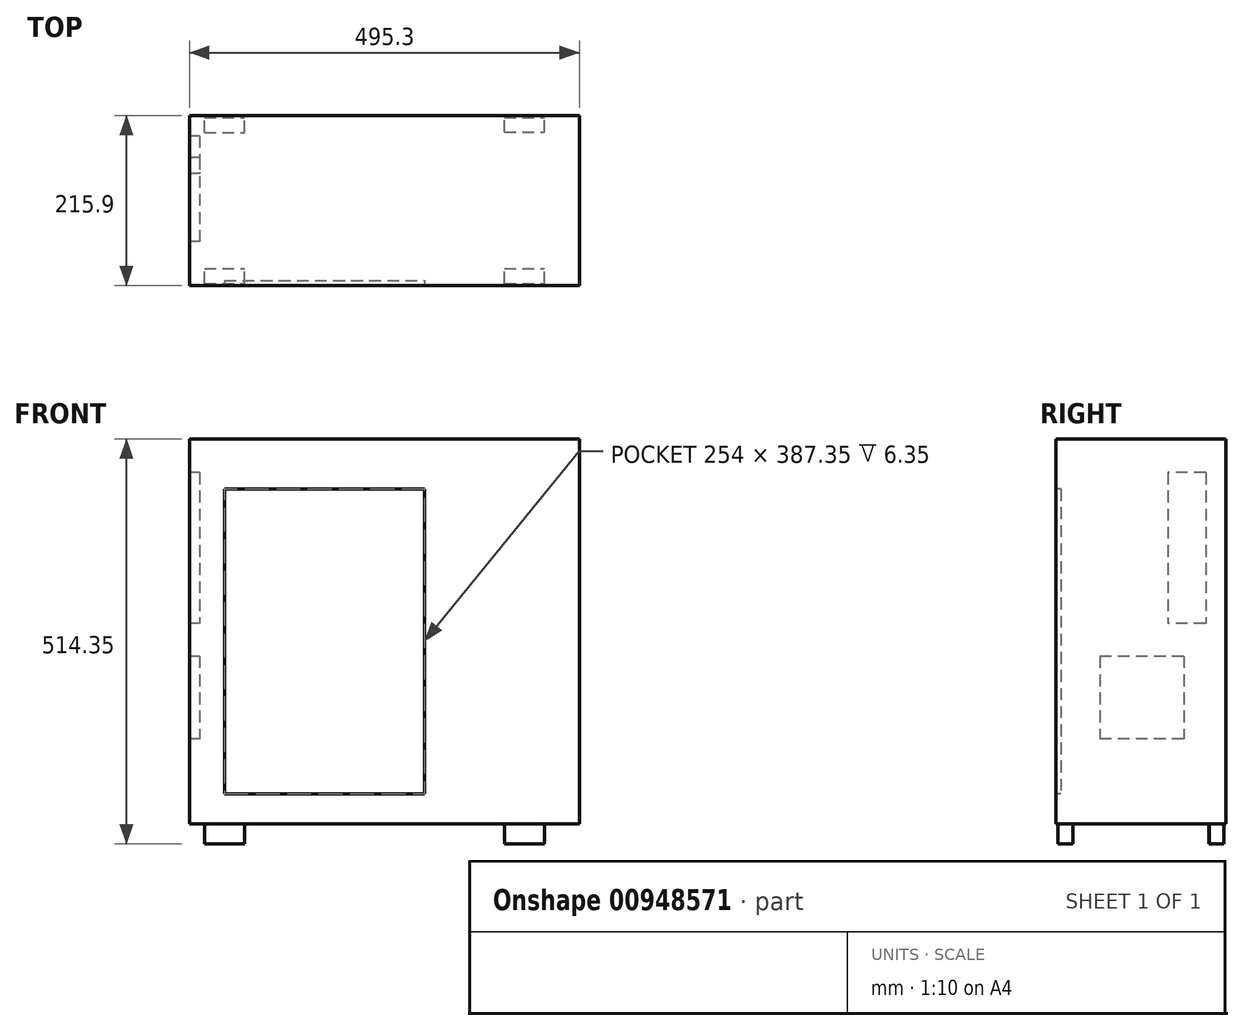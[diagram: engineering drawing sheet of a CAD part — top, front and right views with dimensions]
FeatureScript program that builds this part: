
annotation { "Feature Type Name" : "Feature", "Feature Type Description" : "" }
export const myFeature = defineFeature(function(context is Context, id is Id, definition is map)
    precondition{}
    {
        {
            var Q0;
            Q0=qCreatedBy(makeId("Front.planeOp"),FACE);
            var sketch = newSketch(context, id + "F0", { "sketchPlane" : qUnion([Q0])});
            skLineSegment(sketch, "E0.bottom", {"start": v(247.65, 244.47) * mm, "end": v(-247.65, 244.47) * mm});
            skLineSegment(sketch, "E0.top", {"start": v(247.65, -244.48) * mm, "end": v(-247.65, -244.48) * mm});
            skLineSegment(sketch, "E0.left", {"start": v(247.65, 244.47) * mm, "end": v(247.65, -244.48) * mm});
            skLineSegment(sketch, "E0.right", {"start": v(-247.65, 244.48) * mm, "end": v(-247.65, -244.47) * mm});
            skPoint(sketch, "E0.middle", {"position": v(0, 0) * mm});
            skSolve(sketch);
        }
        {
            var Q0;
            Q0=makeQuery(id+"F0.imprint","IMPRINT",FACE,{"disambiguationData":[TD([[makeQuery(id+"F0.imprint","IMPRINT",EDGE,{"derivedFrom":sQuery(id+"F0.wireOp",EDGE,"E0.bottom")}),1.0]])]});
            extrude(context, id + "F1", {"entities" : qUnion([Q0]), "depth" : 215.9 * mm, "offsetDistance" : 25.4 * mm, "symmetric" : true});
        }
        {
            var Q0;
            Q0=makeQuery(id+"F1.opExtrude","CAP_FACE",FACE,{"disambiguationData":[OSD([sQuery(id+"F0.wireOp",EDGE,"E0.bottom"),sQuery(id+"F0.wireOp",EDGE,"E0.top"),sQuery(id+"F0.wireOp",EDGE,"E0.left"),sQuery(id+"F0.wireOp",EDGE,"E0.right")])],"isStart":false});
            var sketch = newSketch(context, id + "F2", { "sketchPlane" : qUnion([Q0])});
            skLineSegment(sketch, "E1.bottom", {"start": v(-203.2, 180.97) * mm, "end": v(50.8, 180.97) * mm});
            skLineSegment(sketch, "E1.top", {"start": v(-203.2, -206.38) * mm, "end": v(50.8, -206.38) * mm});
            skLineSegment(sketch, "E1.left", {"start": v(-203.2, 180.97) * mm, "end": v(-203.2, -206.38) * mm});
            skLineSegment(sketch, "E1.right", {"start": v(50.8, 180.97) * mm, "end": v(50.8, -206.38) * mm});
            skSolve(sketch);
        }
        {
            var Q0;
            Q0=makeQuery(id+"F2.imprint","IMPRINT",FACE,{"disambiguationData":[TD([[makeQuery(id+"F2.imprint","IMPRINT",EDGE,{"derivedFrom":sQuery(id+"F2.wireOp",EDGE,"E1.bottom")}),-1.0]])]});
            extrude(context, id + "F3", {"entities" : qUnion([Q0]), "operationType" : NewBodyOperationType.REMOVE, "oppositeDirection" : true, "depth" : 6.35 * mm, "offsetDistance" : 25.4 * mm});
        }
        {
            var Q0;
            Q0=makeQuery(id+"F1.opExtrude","SWEPT_FACE",FACE,{"disambiguationData":[OSD([sQuery(id+"F0.wireOp",EDGE,"E0.top")])]});
            var sketch = newSketch(context, id + "F4", { "sketchPlane" : qUnion([Q0])});
            skLineSegment(sketch, "E2.bottom", {"start": v(-228.6, -86.36) * mm, "end": v(-177.8, -86.36) * mm});
            skLineSegment(sketch, "E2.top", {"start": v(-228.6, -105.4) * mm, "end": v(-177.8, -105.4) * mm});
            skLineSegment(sketch, "E2.left", {"start": v(-228.6, -86.36) * mm, "end": v(-228.6, -105.4) * mm});
            skLineSegment(sketch, "E2.right", {"start": v(-177.8, -86.36) * mm, "end": v(-177.8, -105.4) * mm});
            skLineSegment(sketch, "E3.bottom", {"start": v(152.4, -87) * mm, "end": v(203.2, -87) * mm});
            skLineSegment(sketch, "E3.top", {"start": v(152.4, -105.4) * mm, "end": v(203.2, -105.4) * mm});
            skLineSegment(sketch, "E3.left", {"start": v(152.4, -87) * mm, "end": v(152.4, -105.4) * mm});
            skLineSegment(sketch, "E3.right", {"start": v(203.2, -87) * mm, "end": v(203.2, -105.4) * mm});
            skLineSegment(sketch, "E4.bottom", {"start": v(152.4, 105.4) * mm, "end": v(203.2, 105.4) * mm});
            skLineSegment(sketch, "E4.top", {"start": v(152.4, 86.36) * mm, "end": v(203.2, 86.36) * mm});
            skLineSegment(sketch, "E4.left", {"start": v(152.4, 105.4) * mm, "end": v(152.4, 86.36) * mm});
            skLineSegment(sketch, "E4.right", {"start": v(203.2, 105.4) * mm, "end": v(203.2, 86.36) * mm});
            skLineSegment(sketch, "E5.bottom", {"start": v(-228.6, 105.4) * mm, "end": v(-177.8, 105.4) * mm});
            skLineSegment(sketch, "E5.top", {"start": v(-228.6, 86.36) * mm, "end": v(-177.8, 86.36) * mm});
            skLineSegment(sketch, "E5.left", {"start": v(-228.6, 105.4) * mm, "end": v(-228.6, 86.36) * mm});
            skLineSegment(sketch, "E5.right", {"start": v(-177.8, 105.4) * mm, "end": v(-177.8, 86.36) * mm});
            skSolve(sketch);
        }
        {
            var Q0;
            Q0=makeQuery(id+"F4.imprint","IMPRINT",FACE,{"disambiguationData":[TD([[makeQuery(id+"F4.imprint","IMPRINT",EDGE,{"derivedFrom":sQuery(id+"F4.wireOp",EDGE,"E5.bottom")}),-1.0]])]});
            var Q1;
            Q1=makeQuery(id+"F4.imprint","IMPRINT",FACE,{"disambiguationData":[TD([[makeQuery(id+"F4.imprint","IMPRINT",EDGE,{"derivedFrom":sQuery(id+"F4.wireOp",EDGE,"E4.bottom")}),-1.0]])]});
            var Q2;
            Q2=makeQuery(id+"F4.imprint","IMPRINT",FACE,{"disambiguationData":[TD([[makeQuery(id+"F4.imprint","IMPRINT",EDGE,{"derivedFrom":sQuery(id+"F4.wireOp",EDGE,"E3.bottom")}),-1.0]])]});
            var Q3;
            Q3=makeQuery(id+"F4.imprint","IMPRINT",FACE,{"disambiguationData":[TD([[makeQuery(id+"F4.imprint","IMPRINT",EDGE,{"derivedFrom":sQuery(id+"F4.wireOp",EDGE,"E2.bottom")}),-1.0]])]});
            extrude(context, id + "F5", {"entities" : qUnion([Q0, Q1, Q2, Q3]), "operationType" : NewBodyOperationType.ADD, "depth" : 25.4 * mm, "offsetDistance" : 25.4 * mm});
        }
        {
            var Q0;
            Q0=makeQuery(id+"F1.opExtrude","SWEPT_FACE",FACE,{"disambiguationData":[OSD([sQuery(id+"F0.wireOp",EDGE,"E0.right")])]});
            var sketch = newSketch(context, id + "F6", { "sketchPlane" : qUnion([Q0])});
            skLineSegment(sketch, "E6.bottom", {"start": v(-82.06, 201.86) * mm, "end": v(-34.28, 201.86) * mm});
            skLineSegment(sketch, "E6.top", {"start": v(-82.06, 10.04) * mm, "end": v(-34.28, 10.04) * mm});
            skLineSegment(sketch, "E6.left", {"start": v(-82.06, 201.86) * mm, "end": v(-82.06, 10.04) * mm});
            skLineSegment(sketch, "E6.right", {"start": v(-34.28, 201.86) * mm, "end": v(-34.28, 10.04) * mm});
            skLineSegment(sketch, "E7.bottom", {"start": v(-54.36, -31.5) * mm, "end": v(52.28, -31.5) * mm});
            skLineSegment(sketch, "E7.top", {"start": v(-54.36, -136.77) * mm, "end": v(52.28, -136.77) * mm});
            skLineSegment(sketch, "E7.left", {"start": v(-54.36, -31.5) * mm, "end": v(-54.36, -136.77) * mm});
            skLineSegment(sketch, "E7.right", {"start": v(52.28, -31.5) * mm, "end": v(52.28, -136.77) * mm});
            skSolve(sketch);
        }
        {
            var Q0;
            Q0=makeQuery(id+"F6.imprint","IMPRINT",FACE,{"disambiguationData":[TD([[makeQuery(id+"F6.imprint","IMPRINT",EDGE,{"derivedFrom":sQuery(id+"F6.wireOp",EDGE,"E7.bottom")}),-1.0]])]});
            var Q1;
            Q1=makeQuery(id+"F6.imprint","IMPRINT",FACE,{"disambiguationData":[TD([[makeQuery(id+"F6.imprint","IMPRINT",EDGE,{"derivedFrom":sQuery(id+"F6.wireOp",EDGE,"E6.bottom")}),-1.0]])]});
            extrude(context, id + "F7", {"entities" : qUnion([Q0, Q1]), "operationType" : NewBodyOperationType.REMOVE, "oppositeDirection" : true, "depth" : 12.7 * mm, "offsetDistance" : 25.4 * mm});
        }
    });
